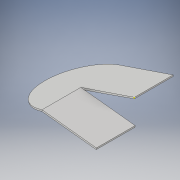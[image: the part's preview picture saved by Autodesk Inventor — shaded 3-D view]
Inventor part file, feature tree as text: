
AUTODESK INVENTOR PART (.ipt)
format: ipt  version: 2017 (Build 210142000, 142)  size: 128,000 bytes
history: native  units: in
note: dims shown in document units (in); Inventor stores cm internally (conversion verified against a paired STEP export)
features: sketch x6, extrude x4, plane x2
ambient origin geometry x8: Origin, YZ Plane, XZ Plane, XY Plane, X Axis, Y Axis, Z Axis, Center Point
bodies: Solid1 (feature_tree)
feature tree (12):
  extrude  "Extrusion1"  Depth=27.2in
  extrude  "Extrusion2"  Depth=1.0in
  sketch  "Sketch4"  dims[d9=3.125in d10=0.0in d11=38.375in d12=0.0in]
  plane  "Work Plane1"
  plane  "Work Plane2"
  extrude  "Extrusion3"  Depth=38.375in TaperAngle=0.0deg
  sketch  "Sketch7"
  extrude  "Extrusion4"  [1 undecoded]
  sketch  "Sketch1"  dims[d2=27.2in d3=0.0in d4=27.2in]
  sketch  "Sketch3"  dims[d5=1.0in d6=0.0in d7=0.4466in d8=-0.5625in]
  sketch  "Sketch6"
  sketch  "Sketch8"
note: 1 required parameter value undecoded (feature->parameter linkage not recoverable at this tier; creation-order binding heuristic only, values carry confidence <= 0.55)
